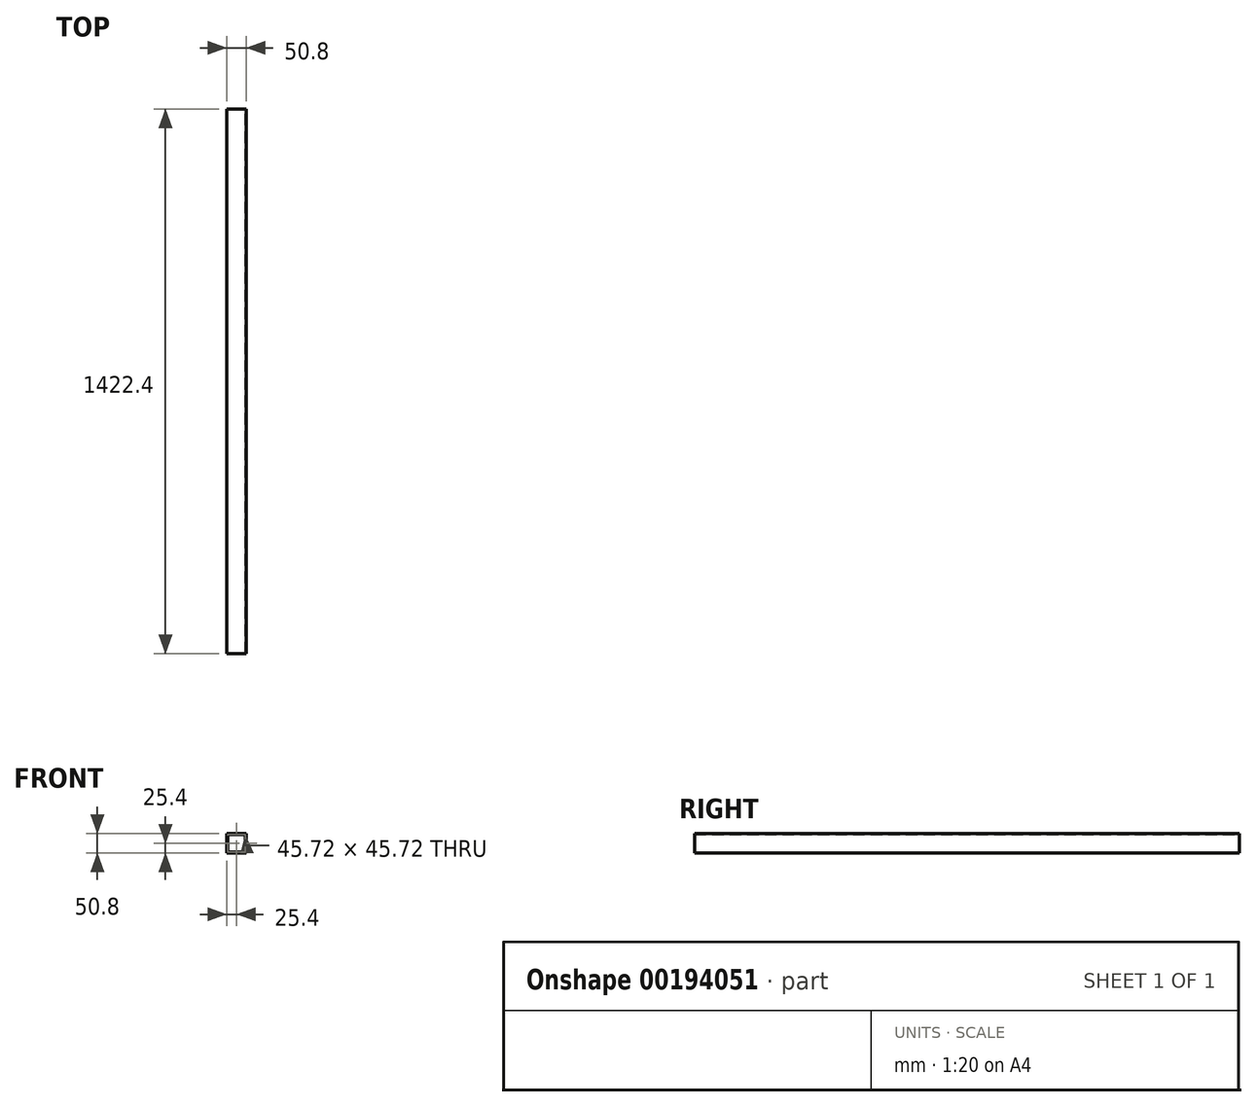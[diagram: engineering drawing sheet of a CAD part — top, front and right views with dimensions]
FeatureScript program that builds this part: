
annotation { "Feature Type Name" : "Feature", "Feature Type Description" : "" }
export const myFeature = defineFeature(function(context is Context, id is Id, definition is map)
    precondition{}
    {
        {
            var Q0;
            Q0=qCreatedBy(makeId("Right.planeOp"),FACE);
            var sketch = newSketch(context, id + "F0", { "sketchPlane" : qUnion([Q0])});
            skLineSegment(sketch, "E0.bottom", {"start": v(-711.2, 25.4) * mm, "end": v(711.2, 25.4) * mm});
            skLineSegment(sketch, "E0.top", {"start": v(-711.2, -25.4) * mm, "end": v(711.2, -25.4) * mm});
            skLineSegment(sketch, "E0.left", {"start": v(-711.2, 25.4) * mm, "end": v(-711.2, -25.4) * mm});
            skLineSegment(sketch, "E0.right", {"start": v(711.2, 25.4) * mm, "end": v(711.2, -25.4) * mm});
            skPoint(sketch, "E0.middle", {"position": v(0, 0) * mm});
            skSolve(sketch);
        }
        {
            var Q0;
            Q0=makeQuery(id+"F0.imprint","IMPRINT",FACE,{"disambiguationData":[TD([[makeQuery(id+"F0.imprint","IMPRINT",EDGE,{"derivedFrom":sQuery(id+"F0.wireOp",EDGE,"E0.bottom")}),-1.0]])]});
            extrude(context, id + "F1", {"entities" : qUnion([Q0]), "depth" : 50.8 * mm});
        }
        {
            var Q0;
            Q0=makeQuery(id+"F1.opExtrude","SWEPT_FACE",FACE,{"disambiguationData":[OSD([sQuery(id+"F0.wireOp",EDGE,"E0.right")])]});
            var Q1;
            Q1=makeQuery(id+"F1.opExtrude","SWEPT_FACE",FACE,{"disambiguationData":[OSD([sQuery(id+"F0.wireOp",EDGE,"E0.left")])]});
            shell(context, id + "F2", {"entities" : qUnion([Q0, Q1]), "thickness" : 2.54 * mm});
        }
    });
